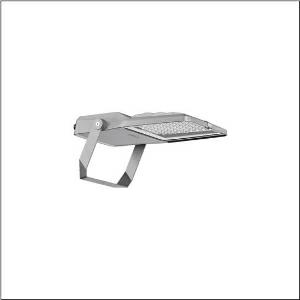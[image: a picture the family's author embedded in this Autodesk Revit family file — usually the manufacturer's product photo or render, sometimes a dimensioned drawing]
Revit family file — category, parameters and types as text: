
# Revit family: floodlight_fl_21_iq_mini___rs12_5xa7772b3b1a_fd5e
name_source: partatom
category: Lighting Fixtures
units: mm (PartAtom-declared; Revit-internal decimal feet)

## family parameters
Cut with Voids When Loaded = No
Host = Face
Light Source = No
Part Type = Normal
Room Calculation Point = No
Round Connector Dimension = Use Diameter
Shared = No

## types (1)
- --- (1 x LED, 5430 lm, 45.5 W, 3000K)
    Apparent Load = 46 VA
    CIE Flux Codes = 79 92 99 100 100
    Color Rendering = 80
    Color Temperature = 3000K
    Default Elevation = 1800 mm
    Description = Floodlight FL 21 iQ mini, floodlight, primary light control with lens, of PMMA, primary optical cover: protective disc, of toughened safety glass, transparent, light distribution: RS12, light emission: direct distribution, installation type: surface-mounted, LED, High Power LED, rated luminous flux: 5.430lm, luminous efficacy: 119lm/W, light colour: 830, colour temperature: 3000K, control gear: iQ Street-Remote/DALI, control: Street-Remote, Auto-Match, Temp-Guard, Night-Set, Smart-Wire, Desk-Remote (wireless, voltage-free reading and setting of iQ features in the workshop via application-optimized NFC function/RFID function), optimised constant luminous flux control (CLO 2.0), with terminal, 6-pole, mains connection: 220..240V, AC, 50/60Hz, start of lifetime: 46W, end of service life: 48W, reduction: 21W, luminaire housing, of diecast aluminium, powder-coated, Siteco® metallic grey (DB 702S), corrosivity category C5 mid according to DIN EN ISO 12944, suitable for swimming pools, chlorine-resistant, sealing non-destructively replaceable, mounting bracket, of steel, galvanised, powder-coated, Siteco® metallic grey (DB 702S), protection rating (complete): IP66, insulation class (complete): insulation class II (safety insulation), certification: CE, ENEC, VDE, protection symbol: D, impact resistance: IK08, permissible operating ambient temperature: -40..+40°C, permissible operating ambient temperature for outdoor applications: -40..+50°C, standard: DIN EN 12944, LABS conformity tested according to VDMA 24364:2018-05, packaging unit: 1 piece

Light Distribution: RS12
    Height = 70 mm
    Lamp = 1 x LED
    Lamp Light Flux = 5430 lm
    Lamp Power = 45.5 W
    Lamp count = 1
    Length = 485 mm
    Luminous efficacy = 119 lm/W
    Manufacturer = Siteco
    ModVariant = No
    Model = 5XA7772B3B1A
    Number of Poles = 1
    OnlyDefault = Yes
    Power Factor = 1
    Product Name = Floodlight FL 21 iQ mini | RS12
    Product group = floodlight | pylon annexe
    ProductGroupID = 6200
    Protection Class = Protection class II
    Protection Degree = IP 66
    RLX_Detail_Level = 1
    RLX_Emergency_Light_Flux = 0 lm
    RLX_Emergency_Type = 0
    RLX_Emergency_Type_DB = No
    RlxData = <blob elided: 91025 chars, md5=4a329331>
    Socket = socket
    Standby Power = 0 W
    System Light Flux = 5430 lm
    System Power = 46 W
    Type Comments = factory setting: luminous flux: 100 % | dim-lin: 254 | 463 mA
    Type Image = l_1006845.jpg
    URL = http://relux.com
    VarID = @adj_167852
    Voltage = 0 V
    Weight = 0.00 kg
    Width = 337 mm

## geometry (parser evidence)
native form markers: Blend x4, Sweep x14
no freeform markers — native parametric forms only
